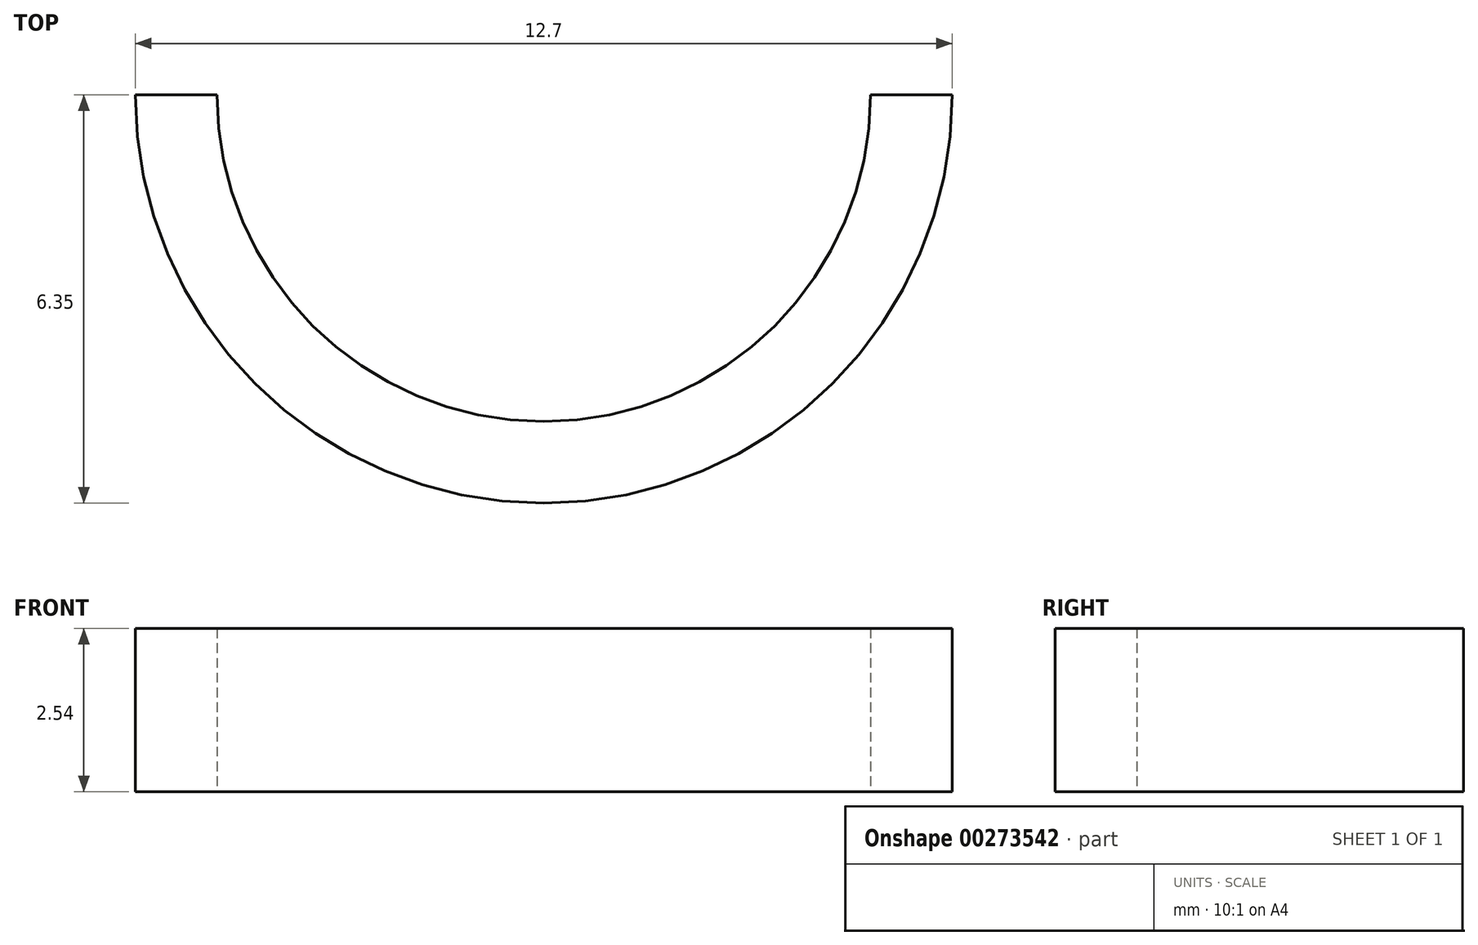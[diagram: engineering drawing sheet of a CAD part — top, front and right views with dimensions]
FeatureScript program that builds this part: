
annotation { "Feature Type Name" : "Feature", "Feature Type Description" : "" }
export const myFeature = defineFeature(function(context is Context, id is Id, definition is map)
    precondition{}
    {
        {
            var Q0;
            Q0=qCreatedBy(makeId("Top.planeOp"),FACE);
            var sketch = newSketch(context, id + "F0", { "sketchPlane" : qUnion([Q0])});
            skArc(sketch, "E0", {"start": v(-6.35, 0) * mm, "mid": v(0, -6.35) * mm, "end": v(6.35, 0) * mm});
            skArc(sketch, "E1", {"start": v(-5.08, 0) * mm, "mid": v(0, -5.08) * mm, "end": v(5.08, 0) * mm});
            skLineSegment(sketch, "E2", {"start": v(-6.35, 0) * mm, "end": v(-5.08, 0) * mm});
            skLineSegment(sketch, "E3.trimOffspring", {"start": v(5.08, 0) * mm, "end": v(6.35, 0) * mm});
            skSolve(sketch);
        }
        {
            var Q0;
            Q0=makeQuery(id+"F0.imprint","IMPRINT",FACE,{"disambiguationData":[TD([[makeQuery(id+"F0.imprint","IMPRINT",EDGE,{"derivedFrom":sQuery(id+"F0.wireOp",EDGE,"E0")}),1.0]])]});
            extrude(context, id + "F1", {"entities" : qUnion([Q0]), "depth" : 2.54 * mm});
        }
    });
